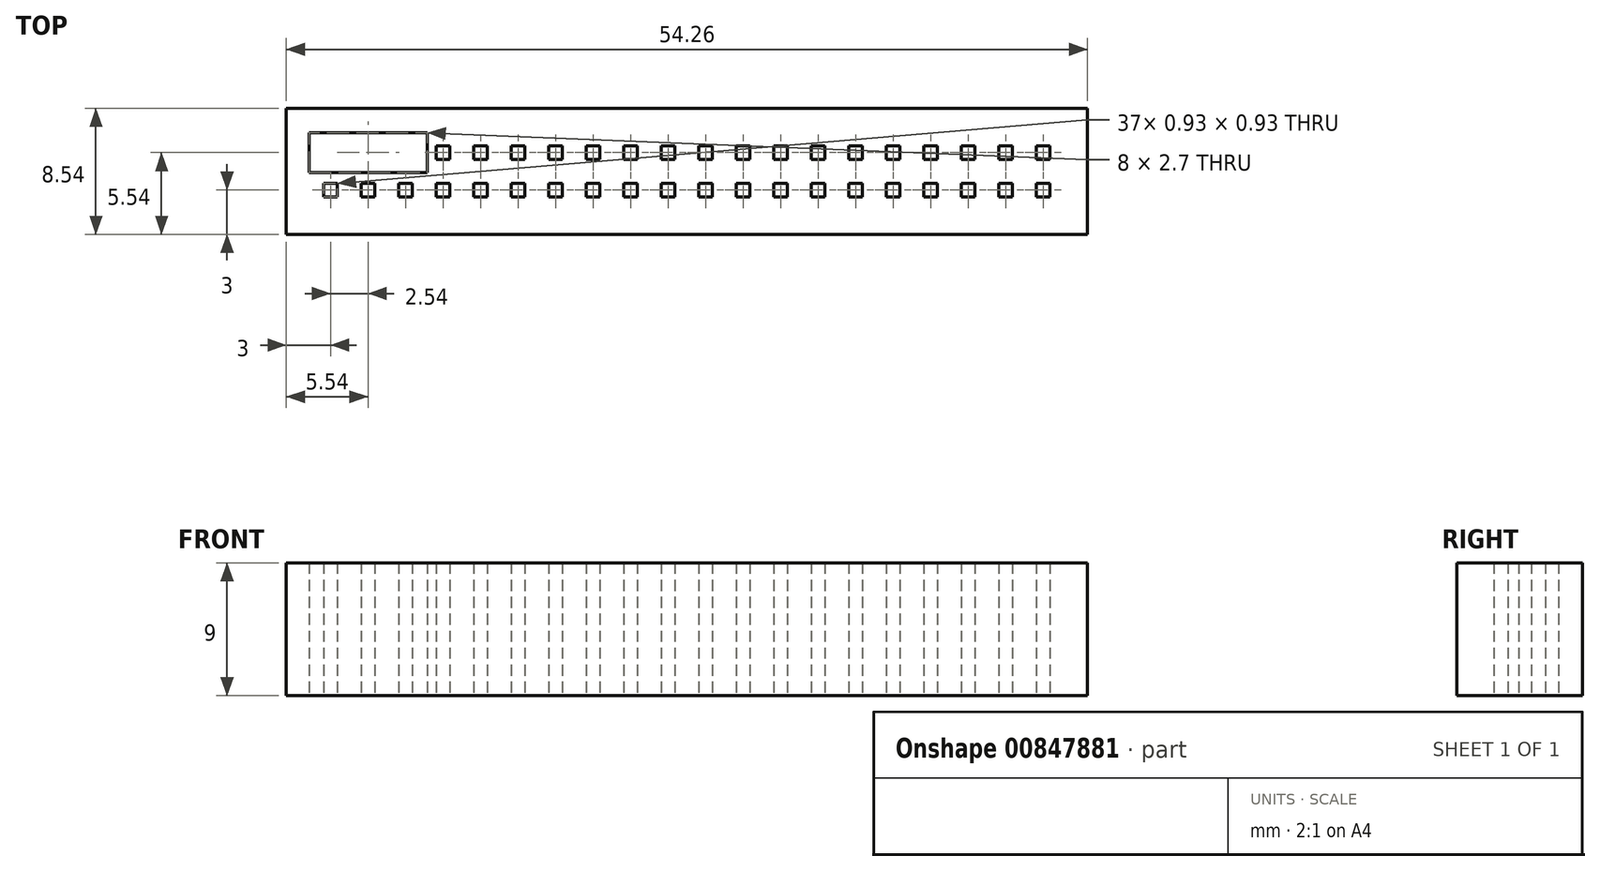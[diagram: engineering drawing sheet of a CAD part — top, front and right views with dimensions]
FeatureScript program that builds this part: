
annotation { "Feature Type Name" : "Feature", "Feature Type Description" : "" }
export const myFeature = defineFeature(function(context is Context, id is Id, definition is map)
    precondition{}
    {
        {
            var Q0;
            Q0=qCreatedBy(makeId("Top.planeOp"),FACE);
            var sketch = newSketch(context, id + "F0", { "sketchPlane" : qUnion([Q0])});
            skLineSegment(sketch, "E0.bottom", {"start": v(-0.47, -0.47) * mm, "end": v(0.47, -0.47) * mm});
            skLineSegment(sketch, "E0.top", {"start": v(-0.47, 0.47) * mm, "end": v(0.47, 0.47) * mm});
            skLineSegment(sketch, "E0.left", {"start": v(-0.47, -0.47) * mm, "end": v(-0.47, 0.47) * mm});
            skLineSegment(sketch, "E0.right", {"start": v(0.47, -0.47) * mm, "end": v(0.47, 0.47) * mm});
            skPoint(sketch, "E0.middle", {"position": v(0, 0) * mm});
            skPoint(sketch, "E1.0.1.0", {"position": v(0, 2.54) * mm});
            skLineSegment(sketch, "E1.0.1.1", {"start": v(-0.47, 2.07) * mm, "end": v(0.47, 2.07) * mm});
            skLineSegment(sketch, "E1.0.1.2", {"start": v(0.47, 2.07) * mm, "end": v(0.47, 3) * mm});
            skLineSegment(sketch, "E1.0.1.3", {"start": v(-0.47, 3) * mm, "end": v(0.47, 3) * mm});
            skLineSegment(sketch, "E1.0.1.4", {"start": v(-0.47, 2.07) * mm, "end": v(-0.47, 3) * mm});
            skPoint(sketch, "E1.1.0.0", {"position": v(2.54, 0) * mm});
            skLineSegment(sketch, "E1.1.0.1", {"start": v(2.07, -0.47) * mm, "end": v(3, -0.47) * mm});
            skLineSegment(sketch, "E1.1.0.2", {"start": v(3, -0.47) * mm, "end": v(3, 0.47) * mm});
            skLineSegment(sketch, "E1.1.0.3", {"start": v(2.07, 0.47) * mm, "end": v(3, 0.47) * mm});
            skLineSegment(sketch, "E1.1.0.4", {"start": v(2.07, -0.47) * mm, "end": v(2.07, 0.47) * mm});
            skPoint(sketch, "E1.1.1.0", {"position": v(2.54, 2.54) * mm});
            skLineSegment(sketch, "E1.1.1.1", {"start": v(2.07, 2.07) * mm, "end": v(3, 2.07) * mm});
            skLineSegment(sketch, "E1.1.1.2", {"start": v(3, 2.07) * mm, "end": v(3, 3) * mm});
            skLineSegment(sketch, "E1.1.1.3", {"start": v(2.07, 3) * mm, "end": v(3, 3) * mm});
            skLineSegment(sketch, "E1.1.1.4", {"start": v(2.07, 2.07) * mm, "end": v(2.07, 3) * mm});
            skPoint(sketch, "E1.2.0.0", {"position": v(5.08, 0) * mm});
            skLineSegment(sketch, "E1.2.0.1", {"start": v(4.61, -0.47) * mm, "end": v(5.55, -0.47) * mm});
            skLineSegment(sketch, "E1.2.0.2", {"start": v(5.55, -0.47) * mm, "end": v(5.55, 0.47) * mm});
            skLineSegment(sketch, "E1.2.0.3", {"start": v(4.61, 0.47) * mm, "end": v(5.55, 0.47) * mm});
            skLineSegment(sketch, "E1.2.0.4", {"start": v(4.61, -0.47) * mm, "end": v(4.61, 0.47) * mm});
            skPoint(sketch, "E1.2.1.0", {"position": v(5.08, 2.54) * mm});
            skLineSegment(sketch, "E1.2.1.1", {"start": v(4.61, 2.07) * mm, "end": v(5.55, 2.07) * mm});
            skLineSegment(sketch, "E1.2.1.2", {"start": v(5.55, 2.07) * mm, "end": v(5.55, 3) * mm});
            skLineSegment(sketch, "E1.2.1.3", {"start": v(4.61, 3) * mm, "end": v(5.55, 3) * mm});
            skLineSegment(sketch, "E1.2.1.4", {"start": v(4.61, 2.07) * mm, "end": v(4.61, 3) * mm});
            skPoint(sketch, "E1.3.0.0", {"position": v(7.62, 0) * mm});
            skLineSegment(sketch, "E1.3.0.1", {"start": v(7.15, -0.47) * mm, "end": v(8.09, -0.47) * mm});
            skLineSegment(sketch, "E1.3.0.2", {"start": v(8.09, -0.47) * mm, "end": v(8.09, 0.47) * mm});
            skLineSegment(sketch, "E1.3.0.3", {"start": v(7.15, 0.47) * mm, "end": v(8.09, 0.47) * mm});
            skLineSegment(sketch, "E1.3.0.4", {"start": v(7.15, -0.47) * mm, "end": v(7.15, 0.47) * mm});
            skPoint(sketch, "E1.3.1.0", {"position": v(7.62, 2.54) * mm});
            skLineSegment(sketch, "E1.3.1.1", {"start": v(7.15, 2.07) * mm, "end": v(8.09, 2.07) * mm});
            skLineSegment(sketch, "E1.3.1.2", {"start": v(8.09, 2.07) * mm, "end": v(8.09, 3) * mm});
            skLineSegment(sketch, "E1.3.1.3", {"start": v(7.15, 3) * mm, "end": v(8.09, 3) * mm});
            skLineSegment(sketch, "E1.3.1.4", {"start": v(7.15, 2.07) * mm, "end": v(7.15, 3) * mm});
            skPoint(sketch, "E1.4.0.0", {"position": v(10.16, 0) * mm});
            skLineSegment(sketch, "E1.4.0.1", {"start": v(9.7, -0.47) * mm, "end": v(10.63, -0.47) * mm});
            skLineSegment(sketch, "E1.4.0.2", {"start": v(10.63, -0.47) * mm, "end": v(10.63, 0.47) * mm});
            skLineSegment(sketch, "E1.4.0.3", {"start": v(9.7, 0.47) * mm, "end": v(10.63, 0.47) * mm});
            skLineSegment(sketch, "E1.4.0.4", {"start": v(9.7, -0.47) * mm, "end": v(9.7, 0.47) * mm});
            skPoint(sketch, "E1.4.1.0", {"position": v(10.16, 2.54) * mm});
            skLineSegment(sketch, "E1.4.1.1", {"start": v(9.7, 2.07) * mm, "end": v(10.63, 2.07) * mm});
            skLineSegment(sketch, "E1.4.1.2", {"start": v(10.63, 2.07) * mm, "end": v(10.63, 3) * mm});
            skLineSegment(sketch, "E1.4.1.3", {"start": v(9.7, 3) * mm, "end": v(10.63, 3) * mm});
            skLineSegment(sketch, "E1.4.1.4", {"start": v(9.7, 2.07) * mm, "end": v(9.7, 3) * mm});
            skPoint(sketch, "E1.5.0.0", {"position": v(12.7, 0) * mm});
            skLineSegment(sketch, "E1.5.0.1", {"start": v(12.23, -0.47) * mm, "end": v(13.17, -0.47) * mm});
            skLineSegment(sketch, "E1.5.0.2", {"start": v(13.17, -0.47) * mm, "end": v(13.17, 0.47) * mm});
            skLineSegment(sketch, "E1.5.0.3", {"start": v(12.23, 0.47) * mm, "end": v(13.17, 0.47) * mm});
            skLineSegment(sketch, "E1.5.0.4", {"start": v(12.23, -0.47) * mm, "end": v(12.23, 0.47) * mm});
            skPoint(sketch, "E1.5.1.0", {"position": v(12.7, 2.54) * mm});
            skLineSegment(sketch, "E1.5.1.1", {"start": v(12.23, 2.07) * mm, "end": v(13.17, 2.07) * mm});
            skLineSegment(sketch, "E1.5.1.2", {"start": v(13.17, 2.07) * mm, "end": v(13.17, 3) * mm});
            skLineSegment(sketch, "E1.5.1.3", {"start": v(12.23, 3) * mm, "end": v(13.17, 3) * mm});
            skLineSegment(sketch, "E1.5.1.4", {"start": v(12.23, 2.07) * mm, "end": v(12.23, 3) * mm});
            skPoint(sketch, "E1.6.0.0", {"position": v(15.24, 0) * mm});
            skLineSegment(sketch, "E1.6.0.1", {"start": v(14.77, -0.47) * mm, "end": v(15.7, -0.47) * mm});
            skLineSegment(sketch, "E1.6.0.2", {"start": v(15.7, -0.47) * mm, "end": v(15.7, 0.47) * mm});
            skLineSegment(sketch, "E1.6.0.3", {"start": v(14.77, 0.47) * mm, "end": v(15.7, 0.47) * mm});
            skLineSegment(sketch, "E1.6.0.4", {"start": v(14.77, -0.47) * mm, "end": v(14.77, 0.47) * mm});
            skPoint(sketch, "E1.6.1.0", {"position": v(15.24, 2.54) * mm});
            skLineSegment(sketch, "E1.6.1.1", {"start": v(14.77, 2.07) * mm, "end": v(15.7, 2.07) * mm});
            skLineSegment(sketch, "E1.6.1.2", {"start": v(15.7, 2.07) * mm, "end": v(15.7, 3) * mm});
            skLineSegment(sketch, "E1.6.1.3", {"start": v(14.77, 3) * mm, "end": v(15.7, 3) * mm});
            skLineSegment(sketch, "E1.6.1.4", {"start": v(14.77, 2.07) * mm, "end": v(14.77, 3) * mm});
            skPoint(sketch, "E1.7.0.0", {"position": v(17.78, 0) * mm});
            skLineSegment(sketch, "E1.7.0.1", {"start": v(17.31, -0.47) * mm, "end": v(18.25, -0.47) * mm});
            skLineSegment(sketch, "E1.7.0.2", {"start": v(18.25, -0.47) * mm, "end": v(18.25, 0.47) * mm});
            skLineSegment(sketch, "E1.7.0.3", {"start": v(17.31, 0.47) * mm, "end": v(18.25, 0.47) * mm});
            skLineSegment(sketch, "E1.7.0.4", {"start": v(17.31, -0.47) * mm, "end": v(17.31, 0.47) * mm});
            skPoint(sketch, "E1.7.1.0", {"position": v(17.78, 2.54) * mm});
            skLineSegment(sketch, "E1.7.1.1", {"start": v(17.31, 2.07) * mm, "end": v(18.25, 2.07) * mm});
            skLineSegment(sketch, "E1.7.1.2", {"start": v(18.25, 2.07) * mm, "end": v(18.25, 3) * mm});
            skLineSegment(sketch, "E1.7.1.3", {"start": v(17.31, 3) * mm, "end": v(18.25, 3) * mm});
            skLineSegment(sketch, "E1.7.1.4", {"start": v(17.31, 2.07) * mm, "end": v(17.31, 3) * mm});
            skPoint(sketch, "E1.8.0.0", {"position": v(20.32, 0) * mm});
            skLineSegment(sketch, "E1.8.0.1", {"start": v(19.85, -0.47) * mm, "end": v(20.79, -0.47) * mm});
            skLineSegment(sketch, "E1.8.0.2", {"start": v(20.79, -0.47) * mm, "end": v(20.79, 0.47) * mm});
            skLineSegment(sketch, "E1.8.0.3", {"start": v(19.85, 0.47) * mm, "end": v(20.79, 0.47) * mm});
            skLineSegment(sketch, "E1.8.0.4", {"start": v(19.85, -0.47) * mm, "end": v(19.85, 0.47) * mm});
            skPoint(sketch, "E1.8.1.0", {"position": v(20.32, 2.54) * mm});
            skLineSegment(sketch, "E1.8.1.1", {"start": v(19.85, 2.07) * mm, "end": v(20.79, 2.07) * mm});
            skLineSegment(sketch, "E1.8.1.2", {"start": v(20.79, 2.07) * mm, "end": v(20.79, 3) * mm});
            skLineSegment(sketch, "E1.8.1.3", {"start": v(19.85, 3) * mm, "end": v(20.79, 3) * mm});
            skLineSegment(sketch, "E1.8.1.4", {"start": v(19.85, 2.07) * mm, "end": v(19.85, 3) * mm});
            skPoint(sketch, "E1.9.0.0", {"position": v(22.86, 0) * mm});
            skLineSegment(sketch, "E1.9.0.1", {"start": v(22.4, -0.47) * mm, "end": v(23.33, -0.47) * mm});
            skLineSegment(sketch, "E1.9.0.2", {"start": v(23.33, -0.47) * mm, "end": v(23.33, 0.47) * mm});
            skLineSegment(sketch, "E1.9.0.3", {"start": v(22.4, 0.47) * mm, "end": v(23.33, 0.47) * mm});
            skLineSegment(sketch, "E1.9.0.4", {"start": v(22.4, -0.47) * mm, "end": v(22.4, 0.47) * mm});
            skPoint(sketch, "E1.9.1.0", {"position": v(22.86, 2.54) * mm});
            skLineSegment(sketch, "E1.9.1.1", {"start": v(22.4, 2.07) * mm, "end": v(23.33, 2.07) * mm});
            skLineSegment(sketch, "E1.9.1.2", {"start": v(23.33, 2.07) * mm, "end": v(23.33, 3) * mm});
            skLineSegment(sketch, "E1.9.1.3", {"start": v(22.4, 3) * mm, "end": v(23.33, 3) * mm});
            skLineSegment(sketch, "E1.9.1.4", {"start": v(22.4, 2.07) * mm, "end": v(22.4, 3) * mm});
            skPoint(sketch, "E1.10.0.0", {"position": v(25.4, 0) * mm});
            skLineSegment(sketch, "E1.10.0.1", {"start": v(24.93, -0.47) * mm, "end": v(25.87, -0.47) * mm});
            skLineSegment(sketch, "E1.10.0.2", {"start": v(25.87, -0.47) * mm, "end": v(25.87, 0.47) * mm});
            skLineSegment(sketch, "E1.10.0.3", {"start": v(24.93, 0.47) * mm, "end": v(25.87, 0.47) * mm});
            skLineSegment(sketch, "E1.10.0.4", {"start": v(24.93, -0.47) * mm, "end": v(24.93, 0.47) * mm});
            skPoint(sketch, "E1.10.1.0", {"position": v(25.4, 2.54) * mm});
            skLineSegment(sketch, "E1.10.1.1", {"start": v(24.93, 2.07) * mm, "end": v(25.87, 2.07) * mm});
            skLineSegment(sketch, "E1.10.1.2", {"start": v(25.87, 2.07) * mm, "end": v(25.87, 3) * mm});
            skLineSegment(sketch, "E1.10.1.3", {"start": v(24.93, 3) * mm, "end": v(25.87, 3) * mm});
            skLineSegment(sketch, "E1.10.1.4", {"start": v(24.93, 2.07) * mm, "end": v(24.93, 3) * mm});
            skPoint(sketch, "E1.11.0.0", {"position": v(27.94, 0) * mm});
            skLineSegment(sketch, "E1.11.0.1", {"start": v(27.47, -0.47) * mm, "end": v(28.4, -0.47) * mm});
            skLineSegment(sketch, "E1.11.0.2", {"start": v(28.4, -0.47) * mm, "end": v(28.4, 0.47) * mm});
            skLineSegment(sketch, "E1.11.0.3", {"start": v(27.47, 0.47) * mm, "end": v(28.4, 0.47) * mm});
            skLineSegment(sketch, "E1.11.0.4", {"start": v(27.47, -0.47) * mm, "end": v(27.47, 0.47) * mm});
            skPoint(sketch, "E1.11.1.0", {"position": v(27.94, 2.54) * mm});
            skLineSegment(sketch, "E1.11.1.1", {"start": v(27.47, 2.07) * mm, "end": v(28.4, 2.07) * mm});
            skLineSegment(sketch, "E1.11.1.2", {"start": v(28.4, 2.07) * mm, "end": v(28.4, 3) * mm});
            skLineSegment(sketch, "E1.11.1.3", {"start": v(27.47, 3) * mm, "end": v(28.4, 3) * mm});
            skLineSegment(sketch, "E1.11.1.4", {"start": v(27.47, 2.07) * mm, "end": v(27.47, 3) * mm});
            skPoint(sketch, "E1.12.0.0", {"position": v(30.48, 0) * mm});
            skLineSegment(sketch, "E1.12.0.1", {"start": v(30.01, -0.47) * mm, "end": v(30.95, -0.47) * mm});
            skLineSegment(sketch, "E1.12.0.2", {"start": v(30.95, -0.47) * mm, "end": v(30.95, 0.47) * mm});
            skLineSegment(sketch, "E1.12.0.3", {"start": v(30.01, 0.47) * mm, "end": v(30.95, 0.47) * mm});
            skLineSegment(sketch, "E1.12.0.4", {"start": v(30.01, -0.47) * mm, "end": v(30.01, 0.47) * mm});
            skPoint(sketch, "E1.12.1.0", {"position": v(30.48, 2.54) * mm});
            skLineSegment(sketch, "E1.12.1.1", {"start": v(30.01, 2.07) * mm, "end": v(30.95, 2.07) * mm});
            skLineSegment(sketch, "E1.12.1.2", {"start": v(30.95, 2.07) * mm, "end": v(30.95, 3) * mm});
            skLineSegment(sketch, "E1.12.1.3", {"start": v(30.01, 3) * mm, "end": v(30.95, 3) * mm});
            skLineSegment(sketch, "E1.12.1.4", {"start": v(30.01, 2.07) * mm, "end": v(30.01, 3) * mm});
            skPoint(sketch, "E1.13.0.0", {"position": v(33.02, 0) * mm});
            skLineSegment(sketch, "E1.13.0.1", {"start": v(32.55, -0.47) * mm, "end": v(33.49, -0.47) * mm});
            skLineSegment(sketch, "E1.13.0.2", {"start": v(33.49, -0.47) * mm, "end": v(33.49, 0.47) * mm});
            skLineSegment(sketch, "E1.13.0.3", {"start": v(32.55, 0.47) * mm, "end": v(33.49, 0.47) * mm});
            skLineSegment(sketch, "E1.13.0.4", {"start": v(32.55, -0.47) * mm, "end": v(32.55, 0.47) * mm});
            skPoint(sketch, "E1.13.1.0", {"position": v(33.02, 2.54) * mm});
            skLineSegment(sketch, "E1.13.1.1", {"start": v(32.55, 2.07) * mm, "end": v(33.49, 2.07) * mm});
            skLineSegment(sketch, "E1.13.1.2", {"start": v(33.49, 2.07) * mm, "end": v(33.49, 3) * mm});
            skLineSegment(sketch, "E1.13.1.3", {"start": v(32.55, 3) * mm, "end": v(33.49, 3) * mm});
            skLineSegment(sketch, "E1.13.1.4", {"start": v(32.55, 2.07) * mm, "end": v(32.55, 3) * mm});
            skPoint(sketch, "E1.14.0.0", {"position": v(35.56, 0) * mm});
            skLineSegment(sketch, "E1.14.0.1", {"start": v(35.1, -0.47) * mm, "end": v(36.03, -0.47) * mm});
            skLineSegment(sketch, "E1.14.0.2", {"start": v(36.03, -0.47) * mm, "end": v(36.03, 0.47) * mm});
            skLineSegment(sketch, "E1.14.0.3", {"start": v(35.1, 0.47) * mm, "end": v(36.03, 0.47) * mm});
            skLineSegment(sketch, "E1.14.0.4", {"start": v(35.1, -0.47) * mm, "end": v(35.1, 0.47) * mm});
            skPoint(sketch, "E1.14.1.0", {"position": v(35.56, 2.54) * mm});
            skLineSegment(sketch, "E1.14.1.1", {"start": v(35.1, 2.07) * mm, "end": v(36.03, 2.07) * mm});
            skLineSegment(sketch, "E1.14.1.2", {"start": v(36.03, 2.07) * mm, "end": v(36.03, 3) * mm});
            skLineSegment(sketch, "E1.14.1.3", {"start": v(35.1, 3) * mm, "end": v(36.03, 3) * mm});
            skLineSegment(sketch, "E1.14.1.4", {"start": v(35.1, 2.07) * mm, "end": v(35.1, 3) * mm});
            skPoint(sketch, "E1.15.0.0", {"position": v(38.1, 0) * mm});
            skLineSegment(sketch, "E1.15.0.1", {"start": v(37.63, -0.47) * mm, "end": v(38.57, -0.47) * mm});
            skLineSegment(sketch, "E1.15.0.2", {"start": v(38.57, -0.47) * mm, "end": v(38.57, 0.47) * mm});
            skLineSegment(sketch, "E1.15.0.3", {"start": v(37.63, 0.47) * mm, "end": v(38.57, 0.47) * mm});
            skLineSegment(sketch, "E1.15.0.4", {"start": v(37.63, -0.47) * mm, "end": v(37.63, 0.47) * mm});
            skPoint(sketch, "E1.15.1.0", {"position": v(38.1, 2.54) * mm});
            skLineSegment(sketch, "E1.15.1.1", {"start": v(37.63, 2.07) * mm, "end": v(38.57, 2.07) * mm});
            skLineSegment(sketch, "E1.15.1.2", {"start": v(38.57, 2.07) * mm, "end": v(38.57, 3) * mm});
            skLineSegment(sketch, "E1.15.1.3", {"start": v(37.63, 3) * mm, "end": v(38.57, 3) * mm});
            skLineSegment(sketch, "E1.15.1.4", {"start": v(37.63, 2.07) * mm, "end": v(37.63, 3) * mm});
            skPoint(sketch, "E1.16.0.0", {"position": v(40.64, 0) * mm});
            skLineSegment(sketch, "E1.16.0.1", {"start": v(40.17, -0.47) * mm, "end": v(41.1, -0.47) * mm});
            skLineSegment(sketch, "E1.16.0.2", {"start": v(41.1, -0.47) * mm, "end": v(41.1, 0.47) * mm});
            skLineSegment(sketch, "E1.16.0.3", {"start": v(40.17, 0.47) * mm, "end": v(41.1, 0.47) * mm});
            skLineSegment(sketch, "E1.16.0.4", {"start": v(40.17, -0.47) * mm, "end": v(40.17, 0.47) * mm});
            skPoint(sketch, "E1.16.1.0", {"position": v(40.64, 2.54) * mm});
            skLineSegment(sketch, "E1.16.1.1", {"start": v(40.17, 2.07) * mm, "end": v(41.1, 2.07) * mm});
            skLineSegment(sketch, "E1.16.1.2", {"start": v(41.1, 2.07) * mm, "end": v(41.1, 3) * mm});
            skLineSegment(sketch, "E1.16.1.3", {"start": v(40.17, 3) * mm, "end": v(41.1, 3) * mm});
            skLineSegment(sketch, "E1.16.1.4", {"start": v(40.17, 2.07) * mm, "end": v(40.17, 3) * mm});
            skPoint(sketch, "E1.17.0.0", {"position": v(43.18, 0) * mm});
            skLineSegment(sketch, "E1.17.0.1", {"start": v(42.71, -0.47) * mm, "end": v(43.65, -0.47) * mm});
            skLineSegment(sketch, "E1.17.0.2", {"start": v(43.65, -0.47) * mm, "end": v(43.65, 0.47) * mm});
            skLineSegment(sketch, "E1.17.0.3", {"start": v(42.71, 0.47) * mm, "end": v(43.65, 0.47) * mm});
            skLineSegment(sketch, "E1.17.0.4", {"start": v(42.71, -0.47) * mm, "end": v(42.71, 0.47) * mm});
            skPoint(sketch, "E1.17.1.0", {"position": v(43.18, 2.54) * mm});
            skLineSegment(sketch, "E1.17.1.1", {"start": v(42.71, 2.07) * mm, "end": v(43.65, 2.07) * mm});
            skLineSegment(sketch, "E1.17.1.2", {"start": v(43.65, 2.07) * mm, "end": v(43.65, 3) * mm});
            skLineSegment(sketch, "E1.17.1.3", {"start": v(42.71, 3) * mm, "end": v(43.65, 3) * mm});
            skLineSegment(sketch, "E1.17.1.4", {"start": v(42.71, 2.07) * mm, "end": v(42.71, 3) * mm});
            skPoint(sketch, "E1.18.0.0", {"position": v(45.72, 0) * mm});
            skLineSegment(sketch, "E1.18.0.1", {"start": v(45.25, -0.47) * mm, "end": v(46.19, -0.47) * mm});
            skLineSegment(sketch, "E1.18.0.2", {"start": v(46.19, -0.47) * mm, "end": v(46.19, 0.47) * mm});
            skLineSegment(sketch, "E1.18.0.3", {"start": v(45.25, 0.47) * mm, "end": v(46.19, 0.47) * mm});
            skLineSegment(sketch, "E1.18.0.4", {"start": v(45.25, -0.47) * mm, "end": v(45.25, 0.47) * mm});
            skPoint(sketch, "E1.18.1.0", {"position": v(45.72, 2.54) * mm});
            skLineSegment(sketch, "E1.18.1.1", {"start": v(45.25, 2.07) * mm, "end": v(46.19, 2.07) * mm});
            skLineSegment(sketch, "E1.18.1.2", {"start": v(46.19, 2.07) * mm, "end": v(46.19, 3) * mm});
            skLineSegment(sketch, "E1.18.1.3", {"start": v(45.25, 3) * mm, "end": v(46.19, 3) * mm});
            skLineSegment(sketch, "E1.18.1.4", {"start": v(45.25, 2.07) * mm, "end": v(45.25, 3) * mm});
            skPoint(sketch, "E1.19.0.0", {"position": v(48.26, 0) * mm});
            skLineSegment(sketch, "E1.19.0.1", {"start": v(47.8, -0.47) * mm, "end": v(48.73, -0.47) * mm});
            skLineSegment(sketch, "E1.19.0.2", {"start": v(48.73, -0.47) * mm, "end": v(48.73, 0.47) * mm});
            skLineSegment(sketch, "E1.19.0.3", {"start": v(47.8, 0.47) * mm, "end": v(48.73, 0.47) * mm});
            skLineSegment(sketch, "E1.19.0.4", {"start": v(47.8, -0.47) * mm, "end": v(47.8, 0.47) * mm});
            skPoint(sketch, "E1.19.1.0", {"position": v(48.26, 2.54) * mm});
            skLineSegment(sketch, "E1.19.1.1", {"start": v(47.8, 2.07) * mm, "end": v(48.73, 2.07) * mm});
            skLineSegment(sketch, "E1.19.1.2", {"start": v(48.73, 2.07) * mm, "end": v(48.73, 3) * mm});
            skLineSegment(sketch, "E1.19.1.3", {"start": v(47.8, 3) * mm, "end": v(48.73, 3) * mm});
            skLineSegment(sketch, "E1.19.1.4", {"start": v(47.8, 2.07) * mm, "end": v(47.8, 3) * mm});
            skLineSegment(sketch, "E1.direction1", {"start": v(-0.47, -0.47) * mm, "end": v(2.07, -0.47) * mm, "construction": true});
            skLineSegment(sketch, "E1.direction2", {"start": v(-0.47, -0.47) * mm, "end": v(-0.47, 2.07) * mm, "construction": true});
            skLineSegment(sketch, "E2.bottom", {"start": v(-3, -3) * mm, "end": v(51.26, -3) * mm});
            skLineSegment(sketch, "E2.top", {"start": v(-3, 5.54) * mm, "end": v(51.26, 5.54) * mm});
            skLineSegment(sketch, "E2.left", {"start": v(-3, -3) * mm, "end": v(-3, 5.54) * mm});
            skLineSegment(sketch, "E2.right", {"start": v(51.26, -3) * mm, "end": v(51.26, 5.54) * mm});
            skLineSegment(sketch, "E3", {"start": v(-0.47, -0.47) * mm, "end": v(0.47, 0.47) * mm, "construction": true});
            skSolve(sketch);
        }
        {
            var Q0;
            Q0=makeQuery(id+"F0.imprint","IMPRINT",FACE,{"disambiguationData":[TD([[makeQuery(id+"F0.imprint","IMPRINT",EDGE,{"derivedFrom":sQuery(id+"F0.wireOp",EDGE,"E0.bottom")}),-1.0]])]});
            extrude(context, id + "F1", {"entities" : qUnion([Q0]), "depth" : 9 * mm, "offsetDistance" : 25 * mm});
        }
        {
            var Q0;
            Q0=qCreatedBy(makeId("Top.planeOp"),FACE);
            var sketch = newSketch(context, id + "F2", { "sketchPlane" : qUnion([Q0])});
            skLineSegment(sketch, "E4.bottom", {"start": v(6.54, 3.9) * mm, "end": v(-1.46, 3.89) * mm});
            skLineSegment(sketch, "E4.top", {"start": v(6.54, 1.19) * mm, "end": v(-1.46, 1.19) * mm});
            skLineSegment(sketch, "E4.left", {"start": v(6.54, 3.9) * mm, "end": v(6.54, 1.19) * mm});
            skLineSegment(sketch, "E4.right", {"start": v(-1.46, 3.89) * mm, "end": v(-1.46, 1.19) * mm});
            skPoint(sketch, "E4.middle", {"position": v(2.54, 2.54) * mm});
            skLineSegment(sketch, "E5.0", {"start": v(2.07, 3) * mm, "end": v(3, 3) * mm});
            skLineSegment(sketch, "E6.0", {"start": v(2.07, 2.07) * mm, "end": v(3, 2.07) * mm});
            skLineSegment(sketch, "E7", {"start": v(2.54, 3) * mm, "end": v(2.54, 2.07) * mm, "construction": true});
            skPoint(sketch, "E7.endSnap0", {"position": v(2.54, 2.07) * mm});
            skSolve(sketch);
        }
        {
            var Q0;
            Q0 = qSketchRegion(id + "F2", true);
            extrude(context, id + "F3", {"entities" : qUnion([Q0]), "operationType" : NewBodyOperationType.REMOVE, "depth" : 25 * mm, "offsetDistance" : 25 * mm});
        }
    });
